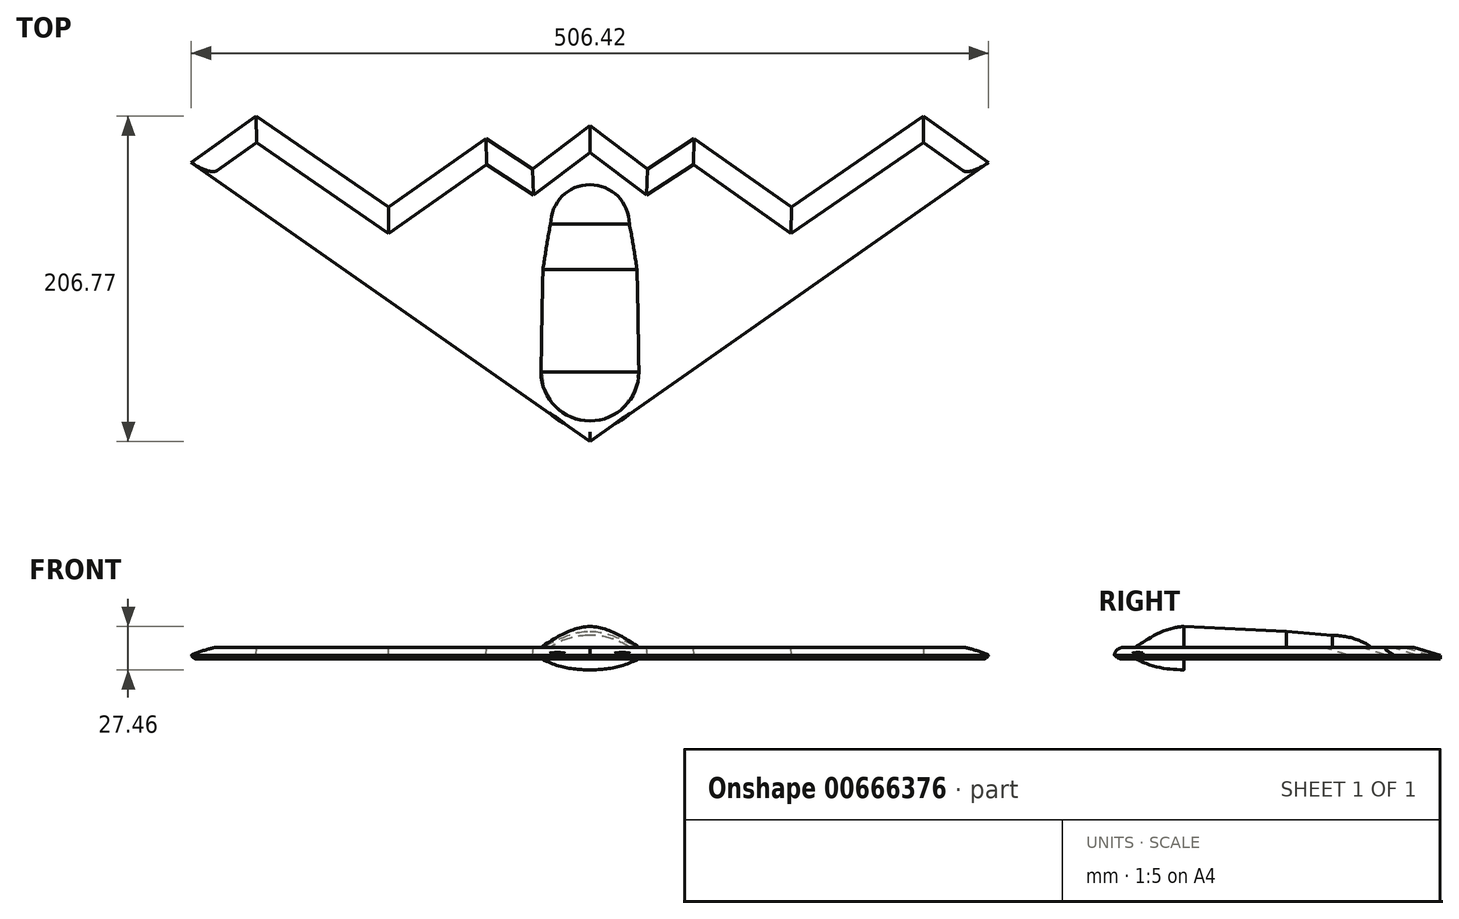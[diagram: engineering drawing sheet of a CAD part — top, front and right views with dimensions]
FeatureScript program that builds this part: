
annotation { "Feature Type Name" : "Feature", "Feature Type Description" : "" }
export const myFeature = defineFeature(function(context is Context, id is Id, definition is map)
    precondition{}
    {
        {
            var Q0;
            Q0=qCreatedBy(makeId("Top.planeOp"),FACE);
            var sketch = newSketch(context, id + "F0", { "sketchPlane" : qUnion([Q0])});
            skLineSegment(sketch, "E0", {"start": v(0, -91.6) * mm, "end": v(36.52, -64.08) * mm});
            skLineSegment(sketch, "E1", {"start": v(36.52, -64.08) * mm, "end": v(66.13, -83.24) * mm});
            skLineSegment(sketch, "E2", {"start": v(66.13, -83.24) * mm, "end": v(127.88, -39.85) * mm});
            skLineSegment(sketch, "E3", {"start": v(127.88, -39.85) * mm, "end": v(211.9, -97.6) * mm});
            skLineSegment(sketch, "E4", {"start": v(211.9, -97.6) * mm, "end": v(253.21, -68.13) * mm});
            skLineSegment(sketch, "E5", {"start": v(253.21, -68.13) * mm, "end": v(0, 109.17) * mm});
            skPoint(sketch, "E6.orphan", {"position": v(0, 97.6) * mm});
            skLineSegment(sketch, "E7.MirrorCS", {"start": v(0, -91.6) * mm, "end": v(-36.52, -64.08) * mm});
            skLineSegment(sketch, "E8.MirrorCS", {"start": v(-36.52, -64.08) * mm, "end": v(-66.13, -83.24) * mm});
            skLineSegment(sketch, "E9.MirrorCS", {"start": v(-66.13, -83.24) * mm, "end": v(-127.88, -39.85) * mm});
            skLineSegment(sketch, "E10.MirrorCS", {"start": v(-127.88, -39.85) * mm, "end": v(-211.9, -97.6) * mm});
            skLineSegment(sketch, "E11.MirrorCS", {"start": v(-211.9, -97.6) * mm, "end": v(-253.21, -68.13) * mm});
            skLineSegment(sketch, "E12.MirrorCS", {"start": v(-253.21, -68.13) * mm, "end": v(0, 109.17) * mm});
            skPoint(sketch, "E13.orphan", {"position": v(-3.96, 111.94) * mm});
            skPoint(sketch, "E14.orphan", {"position": v(3.96, 111.94) * mm});
            skLineSegment(sketch, "E15", {"start": v(-93.4, -64.08) * mm, "end": v(93.4, -64.08) * mm, "construction": true});
            skLineSegment(sketch, "E16.trimOffspring", {"start": v(0, 97.6) * mm, "end": v(0, 109.17) * mm, "construction": true});
            skPoint(sketch, "E17.start.orphan", {"position": v(0, -97.6) * mm});
            skLineSegment(sketch, "E18", {"start": v(0, -91.6) * mm, "end": v(0, 109.17) * mm});
            skLineSegment(sketch, "E19", {"start": v(36.52, -64.08) * mm, "end": v(36.52, 83.6) * mm, "construction": true});
            skLineSegment(sketch, "E20", {"start": v(-36.52, -64.08) * mm, "end": v(-36.52, 83.6) * mm, "construction": true});
            skSolve(sketch);
        }
        {
            var Q0;
            Q0=qCreatedBy(makeId("Right.planeOp"),FACE);
            var sketch = newSketch(context, id + "F1", { "sketchPlane" : qUnion([Q0])});
            skLineSegment(sketch, "E21", {"start": v(100, -20) * mm, "end": v(96.87, -20) * mm, "construction": true});
            skPoint(sketch, "E22.0", {"position": v(109.17, 0) * mm});
            skFitSpline(sketch, "E23", {"points": [v(102.18, 0) * mm, v(96.4, -4.11) * mm, v(90, -5.14) * mm, v(67.6, -16.91) * mm, v(34.25, -16.06) * mm, v(1.83, -13.93) * mm, v(-47.86, 0) * mm], "startDerivative": vector(-62.14, -57) * mm, "endDerivative": vector(-91.15, 63.05) * mm});
            skLineSegment(sketch, "E24", {"start": v(-47.86, 0) * mm, "end": v(-91.6, 0) * mm});
            skFitSpline(sketch, "E25", {"points": [v(-91.6, 0) * mm, v(-54.9, 6.94) * mm, v(-27.65, 11.52) * mm, v(58.38, 11.04) * mm, v(77.02, 8.2) * mm, v(93.96, 1.2) * mm, v(96, 0) * mm, v(102.18, 0) * mm], "startDerivative": vector(175.27, 16.5) * mm, "endDerivative": vector(95.85, 5.43) * mm});
            skLineSegment(sketch, "E26", {"start": v(-91.6, 0) * mm, "end": v(-86.98, 3.18) * mm});
            skLineSegment(sketch, "E27", {"start": v(-86.98, 3.18) * mm, "end": v(35.22, 3.1) * mm});
            skLineSegment(sketch, "E28.0", {"start": v(-91.6, 0) * mm, "end": v(109.17, 0) * mm});
            skFitSpline(sketch, "E29", {"points": [v(35.22, 3.1) * mm, v(88.38, 0) * mm], "startDerivative": vector(56.19, 0.82) * mm, "endDerivative": vector(57.74, -4.68) * mm});
            skLineSegment(sketch, "E30", {"start": v(-47.86, 0) * mm, "end": v(-91.6, 0) * mm, "construction": true});
            skPoint(sketch, "E31", {"position": v(-29.18, -7.34) * mm});
            skPoint(sketch, "E32", {"position": v(81.25, -10.11) * mm});
            skSolve(sketch);
        }
        {
            var Q0;
            Q0=makeQuery(id+"F0.imprint","IMPRINT",FACE,{"disambiguationData":[TD([[makeQuery(id+"F0.imprint","IMPRINT",EDGE,{"derivedFrom":sQuery(id+"F0.wireOp",EDGE,"E7.MirrorCS")}),-1.0]])]});
            var Q1;
            Q1=makeQuery(id+"F0.imprint","IMPRINT",FACE,{"disambiguationData":[TD([[makeQuery(id+"F0.imprint","IMPRINT",EDGE,{"derivedFrom":sQuery(id+"F0.wireOp",EDGE,"E0")}),1.0]])]});
            extrude(context, id + "F2", {"entities" : qUnion([Q0, Q1]), "endBound" : BoundingType.SYMMETRIC, "depth" : 7.5 * mm, "offsetDistance" : 25 * mm});
        }
        {
            var Q0;
            Q0=qCreatedBy(makeId("Front.planeOp"),FACE);
            var Q1;
            Q1 = qBodyType(qCreatedBy(id + "F4" ,EDGE), BodyType.WIRE);
            cPlane(context, id + "F3", {"entities" : qUnion([Q0, Q1]), "cplaneType" : CPlaneType.OFFSET, "offset" : 65 * mm, "oppositeDirection" : true, "width" : 150 * mm, "height" : 150 * mm});
        }
        {
            var Q0;
            Q0=qCreatedBy(id+"F3.planeOp",FACE);
            var sketch = newSketch(context, id + "F4", { "sketchPlane" : qUnion([Q0])});
            skPoint(sketch, "E33.0", {"position": v(36.52, 0) * mm});
            skPoint(sketch, "E34.0", {"position": v(-36.52, 0) * mm});
            skPoint(sketch, "E35.0", {"position": v(0, -16.91) * mm});
            skFitSpline(sketch, "E36", {"points": [v(-36.52, 0) * mm, v(0, -16.91) * mm, v(36.52, 0) * mm], "startDerivative": vector(73.04, -50.73) * mm, "endDerivative": vector(73.04, 50.73) * mm});
            skLineSegment(sketch, "E37", {"start": v(-36.52, 0) * mm, "end": v(36.52, 0) * mm});
            skFitSpline(sketch, "E38.MirrorCS", {"points": [v(-36.52, 0) * mm, v(0, 10.55) * mm, v(36.52, 0) * mm], "startDerivative": vector(73.04, 50.73) * mm, "endDerivative": vector(73.04, -50.73) * mm});
            skLineSegment(sketch, "E39", {"start": v(0, -16.91) * mm, "end": v(0, 0) * mm});
            skLineSegment(sketch, "E40", {"start": v(0, 0) * mm, "end": v(0, 10.55) * mm});
            skSolve(sketch);
        }
        {
            var Q0;
            Q0=qCreatedBy(makeId("Front.planeOp"),FACE);
            var sketch = newSketch(context, id + "F5", { "sketchPlane" : qUnion([Q0])});
            skPoint(sketch, "E41.0", {"position": v(-36.52, 0) * mm});
            skPoint(sketch, "E42.0", {"position": v(36.52, 0) * mm});
            skPoint(sketch, "E43.0", {"position": v(0, -13.93) * mm});
            skLineSegment(sketch, "E44", {"start": v(-36.52, 0) * mm, "end": v(36.52, 0) * mm});
            skFitSpline(sketch, "E45", {"points": [v(-36.52, 0) * mm, v(0, -13.93) * mm, v(36.52, 0) * mm], "startDerivative": vector(73.04, -41.8) * mm, "endDerivative": vector(73.04, 41.8) * mm});
            skLineSegment(sketch, "E46", {"start": v(0, 0) * mm, "end": v(0, -13.93) * mm});
            skSolve(sketch);
        }
        {
            var Q0;
            {var subQ3=sQuery(id+"F4.wireOp",EDGE,"E39");Q0=makeQuery(id+"F4.imprint","IMPRINT",FACE,{"disambiguationData":[TD([[makeQuery(id+"F4.imprint","IMPRINT",EDGE,{"derivedFrom":subQ3}),1.0]])]});}
            var Q1;
            Q1=sQuery(id+"F4.wireOp",EDGE,"E39");
            revolve(context, id + "F6", {"operationType" : NewBodyOperationType.ADD, "entities" : qUnion([Q0]), "axis" : qUnion([Q1]), "revolveType" : RevolveType.ONE_DIRECTION, "oppositeDirection" : true, "angle" : 180 * degree});
        }
        {
            var Q1;
            {var subQ3=sQuery(id+"F4.wireOp",EDGE,"E39");Q1=makeQuery(id+"F4.imprint","IMPRINT",FACE,{"disambiguationData":[TD([[makeQuery(id+"F4.imprint","IMPRINT",EDGE,{"derivedFrom":subQ3}),-1.0]])]});}
            var Q2;
            {var subQ3=sQuery(id+"F5.wireOp",EDGE,"E46");Q2=makeQuery(id+"F5.imprint","IMPRINT",FACE,{"disambiguationData":[TD([[makeQuery(id+"F5.imprint","IMPRINT",EDGE,{"derivedFrom":subQ3}),1.0]])]});}
            loft(context, id + "F7", {"operationType" : NewBodyOperationType.ADD, "sheetProfilesArray" : [{ "sheetProfileEntities" : qUnion([Q1]) }, { "sheetProfileEntities" : qUnion([Q2]) }]});
        }
        {
            var Q1;
            {var subQ3=sQuery(id+"F4.wireOp",EDGE,"E39");Q1=makeQuery(id+"F4.imprint","IMPRINT",FACE,{"disambiguationData":[TD([[makeQuery(id+"F4.imprint","IMPRINT",EDGE,{"derivedFrom":subQ3}),1.0]])]});}
            var Q2;
            {var subQ3=sQuery(id+"F5.wireOp",EDGE,"E46");Q2=makeQuery(id+"F5.imprint","IMPRINT",FACE,{"disambiguationData":[TD([[makeQuery(id+"F5.imprint","IMPRINT",EDGE,{"derivedFrom":subQ3}),-1.0]])]});}
            loft(context, id + "F8", {"operationType" : NewBodyOperationType.ADD, "sheetProfilesArray" : [{ "sheetProfileEntities" : qUnion([Q1]) }, { "sheetProfileEntities" : qUnion([Q2]) }]});
        }
        {
            var Q0;
            {var subQ3=sQuery(id+"F4.wireOp",EDGE,"E40");Q0=makeQuery(id+"F4.imprint","IMPRINT",FACE,{"disambiguationData":[TD([[makeQuery(id+"F4.imprint","IMPRINT",EDGE,{"derivedFrom":subQ3}),1.0]])]});}
            var Q1;
            Q1=sQuery(id+"F4.wireOp",EDGE,"E40");
            revolve(context, id + "F9", {"operationType" : NewBodyOperationType.ADD, "entities" : qUnion([Q0]), "axis" : qUnion([Q1]), "revolveType" : RevolveType.ONE_DIRECTION, "oppositeDirection" : true, "angle" : 180 * degree});
        }
        {
            var Q0;
            Q0=makeQuery(id+"F2.opExtrude","CAP_EDGE",EDGE,{"disambiguationData":[OSD([sQuery(id+"F0.wireOp",EDGE,"E5")])],"isStart":true});
            var Q1;
            Q1=makeQuery(id+"F2.opExtrude","CAP_EDGE",EDGE,{"disambiguationData":[OSD([sQuery(id+"F0.wireOp",EDGE,"E12.MirrorCS")])],"isStart":true});
            fillet(context, id + "F10", {"entities" : qUnion([Q0, Q1]), "radius" : 5 * mm, "tangentPropagation" : true, "allowEdgeOverflow" : false});
        }
        {
            var Q0;
            Q0=makeQuery(id+"F2.opExtrude","CAP_EDGE",EDGE,{"disambiguationData":[OSD([sQuery(id+"F0.wireOp",EDGE,"E5")])],"isStart":false});
            var Q1;
            Q1=makeQuery(id+"F2.opExtrude","CAP_EDGE",EDGE,{"disambiguationData":[OSD([sQuery(id+"F0.wireOp",EDGE,"E12.MirrorCS")])],"isStart":false});
            fillet(context, id + "F11", {"entities" : qUnion([Q0, Q1]), "radius" : 5 * mm, "tangentPropagation" : true, "allowEdgeOverflow" : false});
        }
        {
            var Q0;
            Q0=makeQuery(id+"F2.opExtrude","CAP_EDGE",EDGE,{"disambiguationData":[OSD([sQuery(id+"F0.wireOp",EDGE,"E3")])],"isStart":true});
            var Q1;
            Q1=makeQuery(id+"F2.opExtrude","CAP_EDGE",EDGE,{"disambiguationData":[OSD([sQuery(id+"F0.wireOp",EDGE,"E2")])],"isStart":true});
            var Q2;
            Q2=makeQuery(id+"F2.opExtrude","CAP_EDGE",EDGE,{"disambiguationData":[OSD([sQuery(id+"F0.wireOp",EDGE,"E1")])],"isStart":true});
            var Q3;
            Q3=makeQuery(id+"F2.opExtrude","CAP_EDGE",EDGE,{"disambiguationData":[OSD([sQuery(id+"F0.wireOp",EDGE,"E0")])],"isStart":true});
            var Q4;
            Q4=makeQuery(id+"F2.opExtrude","CAP_EDGE",EDGE,{"disambiguationData":[OSD([sQuery(id+"F0.wireOp",EDGE,"E7.MirrorCS")])],"isStart":true});
            var Q5;
            Q5=makeQuery(id+"F2.opExtrude","CAP_EDGE",EDGE,{"disambiguationData":[OSD([sQuery(id+"F0.wireOp",EDGE,"E8.MirrorCS")])],"isStart":true});
            var Q6;
            Q6=makeQuery(id+"F2.opExtrude","CAP_EDGE",EDGE,{"disambiguationData":[OSD([sQuery(id+"F0.wireOp",EDGE,"E9.MirrorCS")])],"isStart":true});
            var Q7;
            Q7=makeQuery(id+"F2.opExtrude","CAP_EDGE",EDGE,{"disambiguationData":[OSD([sQuery(id+"F0.wireOp",EDGE,"E10.MirrorCS")])],"isStart":true});
            var Q8;
            Q8=makeQuery(id+"F2.opExtrude","CAP_EDGE",EDGE,{"disambiguationData":[OSD([sQuery(id+"F0.wireOp",EDGE,"E4")])],"isStart":true});
            var Q9;
            Q9=makeQuery(id+"F2.opExtrude","CAP_EDGE",EDGE,{"disambiguationData":[OSD([sQuery(id+"F0.wireOp",EDGE,"E11.MirrorCS")])],"isStart":true});
            chamfer(context, id + "F12", {"entities" : qUnion([Q0, Q1, Q2, Q3, Q4, Q5, Q6, Q7, Q8, Q9]), "chamferType" : ChamferType.OFFSET_ANGLE, "width" : 5 * mm, "oppositeDirection" : false, "angle" : 70 * degree, "tangentPropagation" : true});
        }
        {
            var Q0;
            Q0=makeQuery(id+"F2.opExtrude","CAP_FACE",FACE,{"disambiguationData":[OSD([sQuery(id+"F0.wireOp",EDGE,"E0"),sQuery(id+"F0.wireOp",EDGE,"E1"),sQuery(id+"F0.wireOp",EDGE,"E2"),sQuery(id+"F0.wireOp",EDGE,"E3"),sQuery(id+"F0.wireOp",EDGE,"E4"),sQuery(id+"F0.wireOp",EDGE,"E5"),sQuery(id+"F0.wireOp",EDGE,"E7.MirrorCS"),sQuery(id+"F0.wireOp",EDGE,"E8.MirrorCS"),sQuery(id+"F0.wireOp",EDGE,"E9.MirrorCS"),sQuery(id+"F0.wireOp",EDGE,"E10.MirrorCS"),sQuery(id+"F0.wireOp",EDGE,"E11.MirrorCS"),sQuery(id+"F0.wireOp",EDGE,"E12.MirrorCS")])],"isStart":true});
            var sketch = newSketch(context, id + "F13", { "sketchPlane" : qUnion([Q0])});
            skFitSpline(sketch, "E47.0", {"points": [v(-36.52, 0) * mm, v(-24.35, 0) * mm, v(0, 0) * mm, v(24.35, 0) * mm, v(36.52, 0) * mm]});
            skLineSegment(sketch, "E48", {"start": v(0, 0) * mm, "end": v(0, 48.65) * mm});
            skLineSegment(sketch, "E49", {"start": v(-25, 29.18) * mm, "end": v(25, 29.18) * mm});
            skSolve(sketch);
        }
        {
            var Q0;
            {var subQ3=sQuery(id+"F5.wireOp",EDGE,"E46");Q0=makeQuery(id+"F5.imprint","IMPRINT",FACE,{"disambiguationData":[TD([[makeQuery(id+"F5.imprint","IMPRINT",EDGE,{"derivedFrom":subQ3}),-1.0]])]});}
            cPlane(context, id + "F14", {"entities" : qUnion([Q0]), "cplaneType" : CPlaneType.OFFSET, "offset" : 29 * mm, "width" : 150 * mm, "height" : 150 * mm});
        }
        {
            var Q0;
            Q0=qCreatedBy(id+"F14.planeOp",FACE);
            var sketch = newSketch(context, id + "F15", { "sketchPlane" : qUnion([Q0])});
            skPoint(sketch, "E50.0", {"position": v(-25, -3.75) * mm});
            skPoint(sketch, "E51.0", {"position": v(25, -3.75) * mm});
            skFitSpline(sketch, "E52", {"points": [v(25, -3.75) * mm, v(0, -11.25) * mm, v(-25, -3.75) * mm], "startDerivative": vector(-50, -35.25) * mm, "endDerivative": vector(-50, 35.25) * mm});
            skLineSegment(sketch, "E53.0", {"start": v(-25, -3.75) * mm, "end": v(25, -3.75) * mm});
            skLineSegment(sketch, "E54", {"start": v(0, -11.25) * mm, "end": v(0, -3.75) * mm});
            skSolve(sketch);
        }
        {
            var Q1;
            {var subQ3=sQuery(id+"F5.wireOp",EDGE,"E46");Q1=makeQuery(id+"F5.imprint","IMPRINT",FACE,{"disambiguationData":[TD([[makeQuery(id+"F5.imprint","IMPRINT",EDGE,{"derivedFrom":subQ3}),1.0]])]});}
            var Q2;
            {var subQ3=sQuery(id+"F15.wireOp",EDGE,"E54");Q2=makeQuery(id+"F15.imprint","IMPRINT",FACE,{"disambiguationData":[TD([[makeQuery(id+"F15.imprint","IMPRINT",EDGE,{"derivedFrom":subQ3}),-1.0]])]});}
            loft(context, id + "F16", {"operationType" : NewBodyOperationType.ADD, "sheetProfilesArray" : [{ "sheetProfileEntities" : qUnion([Q1]) }, { "sheetProfileEntities" : qUnion([Q2]) }]});
        }
        {
            var Q1;
            {var subQ3=sQuery(id+"F5.wireOp",EDGE,"E46");Q1=makeQuery(id+"F5.imprint","IMPRINT",FACE,{"disambiguationData":[TD([[makeQuery(id+"F5.imprint","IMPRINT",EDGE,{"derivedFrom":subQ3}),-1.0]])]});}
            var Q2;
            {var subQ3=sQuery(id+"F15.wireOp",EDGE,"E54");Q2=makeQuery(id+"F15.imprint","IMPRINT",FACE,{"disambiguationData":[TD([[makeQuery(id+"F15.imprint","IMPRINT",EDGE,{"derivedFrom":subQ3}),1.0]])]});}
            loft(context, id + "F17", {"operationType" : NewBodyOperationType.ADD, "sheetProfilesArray" : [{ "sheetProfileEntities" : qUnion([Q1]) }, { "sheetProfileEntities" : qUnion([Q2]) }]});
        }
        {
            var Q0;
            {var subQ3=sQuery(id+"F15.wireOp",EDGE,"E54");Q0=makeQuery(id+"F15.imprint","IMPRINT",FACE,{"disambiguationData":[TD([[makeQuery(id+"F15.imprint","IMPRINT",EDGE,{"derivedFrom":subQ3}),-1.0]])]});}
            var Q1;
            Q1=sQuery(id+"F15.wireOp",EDGE,"E54");
            revolve(context, id + "F18", {"operationType" : NewBodyOperationType.ADD, "entities" : qUnion([Q0]), "axis" : qUnion([Q1]), "revolveType" : RevolveType.ONE_DIRECTION, "oppositeDirection" : true, "angle" : 180 * degree});
        }
        {
            var Q0;
            Q0=makeQuery(id+"F2.opExtrude","SWEPT_BODY",BODY,{"disambiguationData":[OSD([sQuery(id+"F0.wireOp",EDGE,"E0"),sQuery(id+"F0.wireOp",EDGE,"E1"),sQuery(id+"F0.wireOp",EDGE,"E2"),sQuery(id+"F0.wireOp",EDGE,"E3"),sQuery(id+"F0.wireOp",EDGE,"E4"),sQuery(id+"F0.wireOp",EDGE,"E5"),sQuery(id+"F0.wireOp",EDGE,"E7.MirrorCS"),sQuery(id+"F0.wireOp",EDGE,"E8.MirrorCS"),sQuery(id+"F0.wireOp",EDGE,"E9.MirrorCS"),sQuery(id+"F0.wireOp",EDGE,"E10.MirrorCS"),sQuery(id+"F0.wireOp",EDGE,"E11.MirrorCS"),sQuery(id+"F0.wireOp",EDGE,"E12.MirrorCS")])]});
            var Q1;
            Q1=sQuery(id+"F4.wireOp",EDGE,"E37");
            transform(context, id + "F19", {"entities" : qUnion([Q0]), "transformType" : TransformType.ROTATION, "transformAxis" : qUnion([Q1]), "angle" : 180 * degree, "makeCopy" : false});
        }
        {
            var Q0;
            Q0=makeQuery(id+"F2.opExtrude","SWEPT_BODY",BODY,{"disambiguationData":[OSD([sQuery(id+"F0.wireOp",EDGE,"E0"),sQuery(id+"F0.wireOp",EDGE,"E1"),sQuery(id+"F0.wireOp",EDGE,"E2"),sQuery(id+"F0.wireOp",EDGE,"E3"),sQuery(id+"F0.wireOp",EDGE,"E4"),sQuery(id+"F0.wireOp",EDGE,"E5"),sQuery(id+"F0.wireOp",EDGE,"E7.MirrorCS"),sQuery(id+"F0.wireOp",EDGE,"E8.MirrorCS"),sQuery(id+"F0.wireOp",EDGE,"E9.MirrorCS"),sQuery(id+"F0.wireOp",EDGE,"E10.MirrorCS"),sQuery(id+"F0.wireOp",EDGE,"E11.MirrorCS"),sQuery(id+"F0.wireOp",EDGE,"E12.MirrorCS")])]});
            transform(context, id + "F20", {"entities" : qUnion([Q0]), "transformType" : TransformType.TRANSLATION_3D, "dx" : 0 * mm, "dy" : -120 * mm, "dz" : 0 * mm, "makeCopy" : false});
        }
    });
